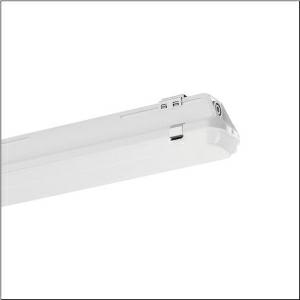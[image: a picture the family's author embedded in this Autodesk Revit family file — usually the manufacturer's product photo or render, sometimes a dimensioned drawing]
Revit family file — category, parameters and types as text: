
# Revit family: monsun_r__21_51fb10dp430b_6f0c
name_source: partatom
category: Lighting Fixtures
units: mm (PartAtom-declared; Revit-internal decimal feet)

## family parameters
Cut with Voids When Loaded = No
Host = Face
Light Source = No
Part Type = Normal
Room Calculation Point = No
Round Connector Dimension = Use Diameter
Shared = No

## types (1)
- --- (1 x LED, 3860 lm, 24.7 W, 4000K)
    Apparent Load = 25 VA
    CIE Flux Codes = 47 77 93 94 100
    Color Rendering = 80
    Color Temperature = 4000K
    Default Elevation = 1800 mm
    Description = Monsun® 21, damp-proof luminaire, chain hanger, primary optical cover: enclosure, of PMMA, light emission: direct distribution, primary light characteristic: symmetric, installation type: suspended mounting, surface-mounted, horizontal mounting, vertical mounting, LED, rated luminous flux: 3.860lm, luminous efficacy: 156lm/W, light colour: 840, colour temperature: 4000K, control gear: ECG DALI, with terminal, 5-pole, max. 2.5mm², mains connection: 220..240V, AC, 50/60Hz, rated input power: 25W, housing, of glass-fibre reinforced polyester, uncoated, bright grey, length: 1.590mm, width: 90mm, height: 88mm, clip for enclosure, of stainless steel (V2A), ceiling mounting element, of stainless steel (V2A), chain hanger, of stainless steel (V2A), protection rating (complete): IP66, insulation class (complete): insulation class I (protective earthing), certification: CE, ENEC, VDE, UKCA, protection symbol: D, impact resistance: IK04, permissible operating ambient temperature: -25..+35°C, standard: EN 50419, EN 60598-2-1, corresponds to IFS (International Featured Standards) requirements for safety and quality in the food industry, for indoor or canopied outdoor use, no direct snow, no direct sun, no direct rain, packaging unit: 1 piece
    Height = 89 mm
    Lamp = 1 x LED
    Lamp Light Flux = 3860 lm
    Lamp Power = 24.7 W
    Lamp count = 1
    Length = 1590 mm
    Luminous efficacy = 156 lm/W
    Manufacturer = Siteco
    ModVariant = No
    Model = 51FB10DP430B
    Mounting Place = Ceiling
    Mounting Type = Pendant
    Number of Poles = 1
    OnlyDefault = Yes
    Power Factor = 1
    Product Name = Monsun® 21
    Product group = damp-proof luminaire | ceiling pendant
    ProductGroupID = 908
    Protection Class = Protection class I
    Protection Degree = IP 66
    RLX_Detail_Level = 1
    RlxData = <blob elided: 92445 chars, md5=36f93ed6>
    Socket = socket
    Standby Power = 0 W
    System Light Flux = 3860 lm
    System Power = 25 W
    Type Comments = factory setting: luminous flux: 100 % | dim-lin: 254 | 162 mA
    Type Image = l_1006717.jpg
    URL = http://relux.com
    VarID = @adj_125291
    Voltage = 0 V
    Weight = 0.00 kg
    Width = 90 mm

## geometry (parser evidence)
native form markers: Blend x4, Sweep x12
no freeform markers — native parametric forms only
